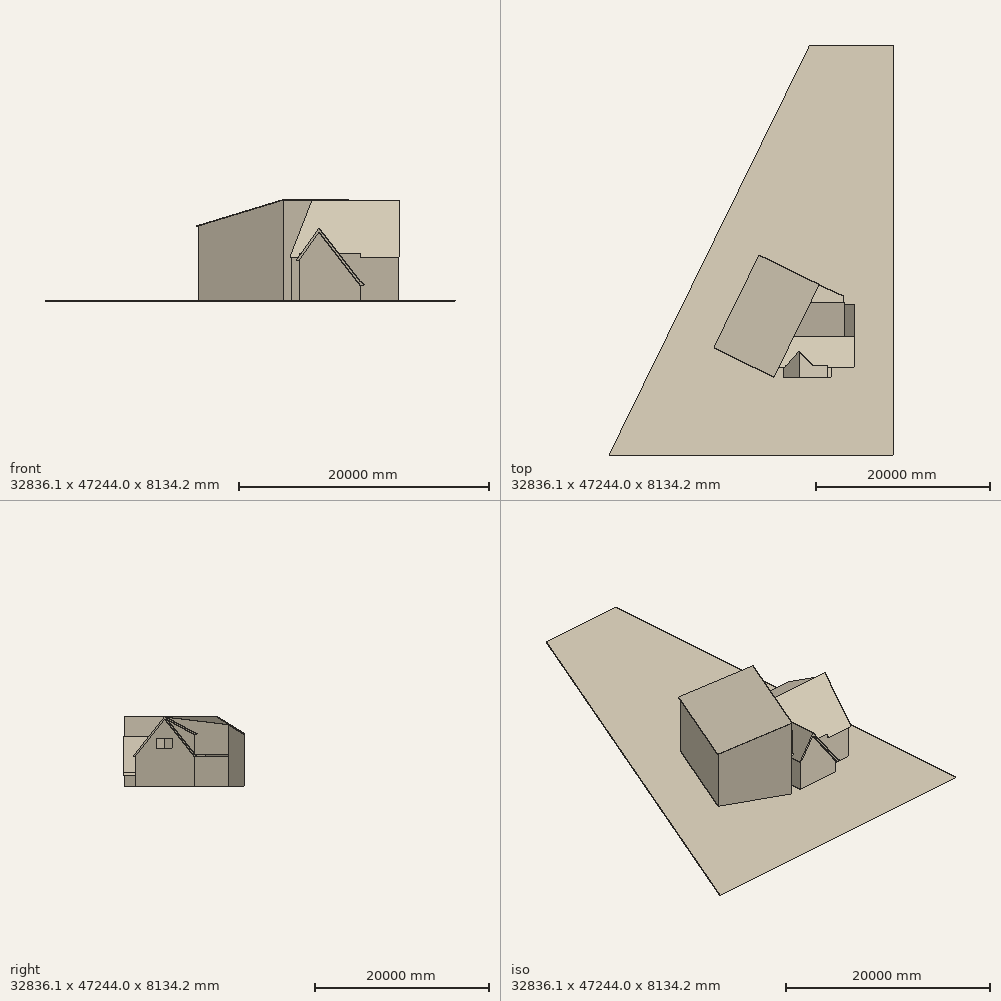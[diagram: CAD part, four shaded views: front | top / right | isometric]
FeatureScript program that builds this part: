
annotation { "Feature Type Name" : "Feature", "Feature Type Description" : "" }
export const myFeature = defineFeature(function(context is Context, id is Id, definition is map)
    precondition{}
    {
        {
            var Q0;
            Q0=qCreatedBy(makeId("Top.planeOp"),FACE);
            var sketch = newSketch(context, id + "F0", { "sketchPlane" : qUnion([Q0])});
            skLineSegment(sketch, "E0", {"start": v(0, 47244) * mm, "end": v(0, 0) * mm});
            skLineSegment(sketch, "E1", {"start": v(0, 0) * mm, "end": v(-32836.1, 0) * mm});
            skLineSegment(sketch, "E2", {"start": v(-32836.1, 0) * mm, "end": v(-9704.83, 47244) * mm});
            skLineSegment(sketch, "E3", {"start": v(-9704.83, 47244) * mm, "end": v(0, 47244) * mm});
            skSolve(sketch);
        }
        {
            var Q0;
            Q0=makeQuery(id+"F0.imprint","IMPRINT",FACE,{"disambiguationData":[TD([[makeQuery(id+"F0.imprint","IMPRINT",EDGE,{"derivedFrom":sQuery(id+"F0.wireOp",EDGE,"E0")}),-1.0]])]});
            extrude(context, id + "F1", {"entities" : qUnion([Q0]), "depth" : 25.4 * mm});
        }
        {
            var Q0;
            Q0=makeQuery(id+"F1.opExtrude","CAP_FACE",FACE,{"disambiguationData":[OSD([sQuery(id+"F0.wireOp",EDGE,"E0"),sQuery(id+"F0.wireOp",EDGE,"E1"),sQuery(id+"F0.wireOp",EDGE,"E2"),sQuery(id+"F0.wireOp",EDGE,"E3")])],"isStart":false});
            var sketch = newSketch(context, id + "F2", { "sketchPlane" : qUnion([Q0])});
            skLineSegment(sketch, "E4.bottom", {"start": v(-13197.84, 17160.24) * mm, "end": v(-4572, 17160.24) * mm});
            skLineSegment(sketch, "E4.top", {"start": v(-13197.84, 10363.2) * mm, "end": v(-4572, 10363.2) * mm});
            skLineSegment(sketch, "E4.left", {"start": v(-13197.84, 17160.24) * mm, "end": v(-13197.84, 10363.2) * mm});
            skLineSegment(sketch, "E4.right", {"start": v(-4572, 17160.24) * mm, "end": v(-4572, 10363.2) * mm});
            skLineSegment(sketch, "E5.bottom", {"start": v(-13045.44, 17007.84) * mm, "end": v(-4724.4, 17007.84) * mm});
            skLineSegment(sketch, "E5.top", {"start": v(-13045.44, 10515.6) * mm, "end": v(-4724.4, 10515.6) * mm});
            skLineSegment(sketch, "E5.left", {"start": v(-13045.44, 17007.84) * mm, "end": v(-13045.44, 10515.6) * mm});
            skLineSegment(sketch, "E5.right", {"start": v(-4724.4, 17007.84) * mm, "end": v(-4724.4, 10515.6) * mm});
            skSolve(sketch);
        }
        {
            var Q0;
            Q0=makeQuery(id+"F2.imprint","IMPRINT",FACE,{"disambiguationData":[TD([[makeQuery(id+"F2.imprint","IMPRINT",EDGE,{"derivedFrom":sQuery(id+"F2.wireOp",EDGE,"E4.bottom")}),-1.0]])]});
            extrude(context, id + "F3", {"entities" : qUnion([Q0]), "offsetDistance" : 30.48 * mm, "depth" : 7734 * mm});
        }
        {
            var Q0;
            Q0=makeQuery(id+"F1.opExtrude","CAP_FACE",FACE,{"disambiguationData":[OSD([sQuery(id+"F0.wireOp",EDGE,"E0"),sQuery(id+"F0.wireOp",EDGE,"E1"),sQuery(id+"F0.wireOp",EDGE,"E2"),sQuery(id+"F0.wireOp",EDGE,"E3")])],"isStart":false});
            var sketch = newSketch(context, id + "F4", { "sketchPlane" : qUnion([Q0])});
            skLineSegment(sketch, "E6", {"start": v(-13197.84, 17160.24) * mm, "end": v(-17465.04, 17160.24) * mm});
            skLineSegment(sketch, "E7", {"start": v(-17465.04, 17160.24) * mm, "end": v(-17465.04, 11064.24) * mm});
            skLineSegment(sketch, "E8", {"start": v(-17465.04, 11064.24) * mm, "end": v(-13197.84, 11064.24) * mm});
            skLineSegment(sketch, "E9", {"start": v(-13197.84, 17007.84) * mm, "end": v(-17312.64, 17007.84) * mm});
            skLineSegment(sketch, "E10", {"start": v(-17312.64, 17007.84) * mm, "end": v(-17312.64, 11216.64) * mm});
            skLineSegment(sketch, "E11", {"start": v(-17312.64, 11216.64) * mm, "end": v(-13197.84, 11216.64) * mm});
            skLineSegment(sketch, "E12", {"start": v(-13197.84, 17160.24) * mm, "end": v(-13197.84, 17007.84) * mm});
            skLineSegment(sketch, "E13", {"start": v(-10808.26, 7562.78) * mm, "end": v(-10586.18, 7562.78) * mm});
            skLineSegment(sketch, "E14", {"start": v(-13197.84, 11216.64) * mm, "end": v(-13197.84, 11064.24) * mm});
            skSolve(sketch);
        }
        {
            var Q0;
            Q0=makeQuery(id+"F4.imprint","IMPRINT",FACE,{"disambiguationData":[TD([[makeQuery(id+"F4.imprint","IMPRINT",EDGE,{"derivedFrom":sQuery(id+"F4.wireOp",EDGE,"E6")}),1.0]])]});
            extrude(context, id + "F5", {"entities" : qUnion([Q0]), "depth" : 3048 * mm});
        }
        {
            var Q0;
            Q0=makeQuery(id+"F1.opExtrude","CAP_FACE",FACE,{"disambiguationData":[OSD([sQuery(id+"F0.wireOp",EDGE,"E0"),sQuery(id+"F0.wireOp",EDGE,"E1"),sQuery(id+"F0.wireOp",EDGE,"E2"),sQuery(id+"F0.wireOp",EDGE,"E3")])],"isStart":false});
            var sketch = newSketch(context, id + "F6", { "sketchPlane" : qUnion([Q0])});
            skLineSegment(sketch, "E15", {"start": v(-12496.8, 10363.2) * mm, "end": v(-12496.8, 9144) * mm});
            skLineSegment(sketch, "E16", {"start": v(-12496.8, 9144) * mm, "end": v(-7620, 9144) * mm});
            skLineSegment(sketch, "E17", {"start": v(-7620, 9144) * mm, "end": v(-7620, 10363.2) * mm});
            skLineSegment(sketch, "E18", {"start": v(-7620, 10363.2) * mm, "end": v(-7772.4, 10363.2) * mm});
            skLineSegment(sketch, "E19", {"start": v(-7772.4, 10363.2) * mm, "end": v(-7772.4, 9296.4) * mm});
            skLineSegment(sketch, "E20", {"start": v(-7772.4, 9296.4) * mm, "end": v(-12344.4, 9296.4) * mm});
            skLineSegment(sketch, "E21", {"start": v(-12344.4, 9296.4) * mm, "end": v(-12344.4, 10363.2) * mm});
            skLineSegment(sketch, "E22", {"start": v(-12344.4, 10363.2) * mm, "end": v(-12496.8, 10363.2) * mm});
            skSolve(sketch);
        }
        {
            var Q0;
            Q0=makeQuery(id+"F6.imprint","IMPRINT",FACE,{"disambiguationData":[TD([[makeQuery(id+"F6.imprint","IMPRINT",EDGE,{"derivedFrom":sQuery(id+"F6.wireOp",EDGE,"E15")}),1.0]])]});
            extrude(context, id + "F7", {"entities" : qUnion([Q0]), "offsetDistance" : 30.48 * mm, "depth" : 5486.4 * mm});
        }
        {
            var Q0;
            Q0=makeQuery(id+"F3.opExtrude","SWEPT_FACE",FACE,{"disambiguationData":[OSD([sQuery(id+"F2.wireOp",EDGE,"E4.right")])]});
            var sketch = newSketch(context, id + "F8", { "sketchPlane" : qUnion([Q0])});
            skLineSegment(sketch, "E23", {"start": v(10363.2, 3479.79) * mm, "end": v(13761.72, 7759.4) * mm});
            skLineSegment(sketch, "E24", {"start": v(13761.72, 7759.4) * mm, "end": v(17160.24, 3479.79) * mm});
            skLineSegment(sketch, "E25", {"start": v(10363.2, 3479.79) * mm, "end": v(10363.2, 7759.4) * mm});
            skLineSegment(sketch, "E26", {"start": v(10363.2, 7759.4) * mm, "end": v(17160.24, 7759.4) * mm});
            skLineSegment(sketch, "E27", {"start": v(17160.24, 7759.4) * mm, "end": v(17160.24, 3479.79) * mm});
            skSolve(sketch);
        }
        {
            var Q0;
            {var subQ0=sQuery(id+"F8.wireOp",EDGE,"E24");Q0=makeQuery(id+"F8.imprint","IMPRINT",FACE,{"disambiguationData":[TD([[makeQuery(id+"F8.imprint","IMPRINT",EDGE,{"derivedFrom":subQ0}),1.0]])]});}
            var Q1;
            {var subQ0=sQuery(id+"F8.wireOp",EDGE,"E23");Q1=makeQuery(id+"F8.imprint","IMPRINT",FACE,{"disambiguationData":[TD([[makeQuery(id+"F8.imprint","IMPRINT",EDGE,{"derivedFrom":subQ0}),1.0]])]});}
            var Q2;
            Q2=makeQuery(id+"F3.opExtrude","SWEPT_FACE",FACE,{"disambiguationData":[OSD([sQuery(id+"F2.wireOp",EDGE,"E4.left")])]});
            extrude(context, id + "F9", {"entities" : qUnion([Q0, Q1]), "operationType" : NewBodyOperationType.REMOVE, "endBound" : BoundingType.UP_TO_SURFACE, "oppositeDirection" : true, "depth" : 30.48 * mm, "endBoundEntityFace" : qUnion([Q2]), "offsetDistance" : 30.48 * mm});
        }
        {
            var Q0;
            Q0=makeQuery(id+"F3.opExtrude","SWEPT_FACE",FACE,{"disambiguationData":[OSD([sQuery(id+"F2.wireOp",EDGE,"E4.right")])]});
            var sketch = newSketch(context, id + "F10", { "sketchPlane" : qUnion([Q0])});
            skLineSegment(sketch, "E28", {"start": v(10103.72, 3479.79) * mm, "end": v(13761.72, 8086.14) * mm});
            skLineSegment(sketch, "E29", {"start": v(13761.72, 8086.14) * mm, "end": v(17419.72, 3479.79) * mm});
            skLineSegment(sketch, "E30", {"start": v(17419.72, 3479.79) * mm, "end": v(17160.24, 3479.79) * mm});
            skLineSegment(sketch, "E31", {"start": v(17160.24, 3479.79) * mm, "end": v(13761.72, 7759.4) * mm});
            skLineSegment(sketch, "E32", {"start": v(13761.72, 7759.4) * mm, "end": v(10363.2, 3479.79) * mm});
            skLineSegment(sketch, "E33", {"start": v(10363.2, 3479.79) * mm, "end": v(10103.72, 3479.79) * mm});
            skSolve(sketch);
        }
        {
            var Q0;
            {var subQ6=sQuery(id+"F10.wireOp",EDGE,"E29");var subQ7=sQuery(id+"F10.wireOp",EDGE,"E28");var subQ8=makeQuery(id+"F10.imprint","INTERSECT",VERTEX,{"derivedFrom":[subQ7,subQ6]});Q0=makeQuery(id+"F10.imprint","IMPRINT",FACE,{"disambiguationData":[TD([[makeQuery(id+"F10.imprint","IMPRINT",EDGE,{"disambiguationData":[TD([[subQ8,1.0]])],"derivedFrom":subQ7}),-1.0]])]});}
            extrude(context, id + "F11", {"entities" : qUnion([Q0]), "operationType" : NewBodyOperationType.ADD, "depth" : 76.2 * mm, "offsetDistance" : 30.48 * mm, "hasSecondDirection" : true, "secondDirectionOppositeDirection" : true, "secondDirectionDepth" : 8702.04 * mm});
        }
        {
            var Q0;
            Q0=makeQuery(id+"F7.opExtrude","SWEPT_FACE",FACE,{"disambiguationData":[OSD([sQuery(id+"F6.wireOp",EDGE,"E16")])]});
            var sketch = newSketch(context, id + "F12", { "sketchPlane" : qUnion([Q0])});
            skLineSegment(sketch, "E34", {"start": v(-12496.8, 3276.6) * mm, "end": v(-10922.02, 5511.8) * mm});
            skLineSegment(sketch, "E35", {"start": v(-10922.02, 5511.8) * mm, "end": v(-7620, 1244.6) * mm});
            skLineSegment(sketch, "E36", {"start": v(-7620, 1244.6) * mm, "end": v(-7620, 5511.8) * mm});
            skLineSegment(sketch, "E37", {"start": v(-7620, 5511.8) * mm, "end": v(-12496.8, 5511.8) * mm});
            skLineSegment(sketch, "E38", {"start": v(-12496.8, 5511.8) * mm, "end": v(-12496.8, 3276.6) * mm});
            skSolve(sketch);
        }
        {
            var Q0;
            Q0=qSketchRegion(id+"F12",true);
            var Q1;
            Q1=makeQuery(id+"F7.opExtrude","SWEPT_FACE",FACE,{"disambiguationData":[OSD([sQuery(id+"F6.wireOp",EDGE,"E22")])]});
            var Q2;
            Q2=makeQuery(id+"F3.opExtrude","SWEPT_BODY",BODY,{"disambiguationData":[OSD([sQuery(id+"F2.wireOp",EDGE,"E4.bottom"),sQuery(id+"F2.wireOp",EDGE,"E4.top"),sQuery(id+"F2.wireOp",EDGE,"E4.left"),sQuery(id+"F2.wireOp",EDGE,"E4.right"),sQuery(id+"F2.wireOp",EDGE,"E5.bottom"),sQuery(id+"F2.wireOp",EDGE,"E5.top"),sQuery(id+"F2.wireOp",EDGE,"E5.left"),sQuery(id+"F2.wireOp",EDGE,"E5.right")])]});
            extrude(context, id + "F13", {"entities" : qUnion([Q0]), "operationType" : NewBodyOperationType.REMOVE, "endBound" : BoundingType.UP_TO_SURFACE, "oppositeDirection" : true, "depth" : 30.48 * mm, "endBoundEntityFace" : qUnion([Q1]), "endBoundEntityBody" : qUnion([Q2]), "offsetDistance" : 30.48 * mm});
        }
        {
            var Q0;
            Q0=makeQuery(id+"F7.opExtrude","SWEPT_FACE",FACE,{"disambiguationData":[OSD([sQuery(id+"F6.wireOp",EDGE,"E16")])]});
            var sketch = newSketch(context, id + "F14", { "sketchPlane" : qUnion([Q0])});
            skLineSegment(sketch, "E39", {"start": v(-10922.02, 5511.8) * mm, "end": v(-12496.8, 3276.6) * mm});
            skLineSegment(sketch, "E40", {"start": v(-12496.8, 3276.6) * mm, "end": v(-12730.73, 3276.6) * mm});
            skLineSegment(sketch, "E41", {"start": v(-12730.73, 3276.6) * mm, "end": v(-10922.02, 5843.83) * mm});
            skLineSegment(sketch, "E42", {"start": v(-10922.02, 5843.83) * mm, "end": v(-7670.8, 1642.28) * mm});
            skLineSegment(sketch, "E43", {"start": v(-7670.8, 1642.28) * mm, "end": v(-7213.6, 1244.6) * mm});
            skLineSegment(sketch, "E44", {"start": v(-7213.6, 1244.6) * mm, "end": v(-7620, 1244.6) * mm});
            skLineSegment(sketch, "E45", {"start": v(-7620, 1244.6) * mm, "end": v(-10922.02, 5511.8) * mm});
            skSolve(sketch);
        }
        {
            var Q0;
            Q0=makeQuery(id+"F14.imprint","IMPRINT",FACE,{"disambiguationData":[TD([[makeQuery(id+"F14.imprint","IMPRINT",EDGE,{"derivedFrom":sQuery(id+"F14.wireOp",EDGE,"E39")}),1.0]])]});
            var Q1;
            Q1=makeQuery(id+"F3.opExtrude","SWEPT_BODY",BODY,{"disambiguationData":[OSD([sQuery(id+"F2.wireOp",EDGE,"E4.bottom"),sQuery(id+"F2.wireOp",EDGE,"E4.top"),sQuery(id+"F2.wireOp",EDGE,"E4.left"),sQuery(id+"F2.wireOp",EDGE,"E4.right"),sQuery(id+"F2.wireOp",EDGE,"E5.bottom"),sQuery(id+"F2.wireOp",EDGE,"E5.top"),sQuery(id+"F2.wireOp",EDGE,"E5.left"),sQuery(id+"F2.wireOp",EDGE,"E5.right")])]});
            var Q2;
            Q2=makeQuery(id+"F3.opExtrude","SWEPT_BODY",BODY,{"disambiguationData":[OSD([sQuery(id+"F2.wireOp",EDGE,"E4.bottom"),sQuery(id+"F2.wireOp",EDGE,"E4.top"),sQuery(id+"F2.wireOp",EDGE,"E4.left"),sQuery(id+"F2.wireOp",EDGE,"E4.right"),sQuery(id+"F2.wireOp",EDGE,"E5.bottom"),sQuery(id+"F2.wireOp",EDGE,"E5.top"),sQuery(id+"F2.wireOp",EDGE,"E5.left"),sQuery(id+"F2.wireOp",EDGE,"E5.right")])]});
            extrude(context, id + "F15", {"entities" : qUnion([Q0]), "depth" : 152.4 * mm, "endBoundEntityBody" : qUnion([Q1]), "offsetDistance" : 30.48 * mm, "hasSecondDirection" : true, "secondDirectionBound" : SecondDirectionBoundingType.UP_TO_BODY, "secondDirectionOppositeDirection" : true, "secondDirectionDepth" : 152.4 * mm, "secondDirectionBoundEntityBody" : qUnion([Q2])});
        }
        {
            var Q0;
            Q0=qCreatedBy(makeId("Top.planeOp"),FACE);
            cPlane(context, id + "F16", {"entities" : qUnion([Q0]), "cplaneType" : CPlaneType.OFFSET, "offset" : 12192 * mm, "width" : 152.4 * mm, "height" : 152.4 * mm});
        }
        {
            var Q0;
            Q0=qCreatedBy(id+"F16.planeOp",FACE);
            var sketch = newSketch(context, id + "F17", { "sketchPlane" : qUnion([Q0])});
            skLineSegment(sketch, "E46", {"start": v(-11978.64, 17160.24) * mm, "end": v(-5791.2, 17160.24) * mm});
            skLineSegment(sketch, "E47", {"start": v(-5791.2, 17160.24) * mm, "end": v(-5791.2, 13761.72) * mm});
            skLineSegment(sketch, "E48", {"start": v(-5791.2, 13761.72) * mm, "end": v(-6019.8, 13761.72) * mm});
            skLineSegment(sketch, "E49", {"start": v(-6019.8, 13761.72) * mm, "end": v(-6019.8, 17007.84) * mm});
            skLineSegment(sketch, "E50", {"start": v(-6019.8, 17007.84) * mm, "end": v(-11750.04, 17007.84) * mm});
            skLineSegment(sketch, "E51", {"start": v(-11750.04, 17007.84) * mm, "end": v(-11750.04, 13761.72) * mm});
            skLineSegment(sketch, "E52", {"start": v(-11750.04, 13761.72) * mm, "end": v(-11978.64, 13761.72) * mm});
            skLineSegment(sketch, "E53", {"start": v(-11978.64, 13761.72) * mm, "end": v(-11978.64, 17160.24) * mm});
            skSolve(sketch);
        }
        {
            var Q0;
            Q0=makeQuery(id+"F17.imprint","IMPRINT",FACE,{"disambiguationData":[TD([[makeQuery(id+"F17.imprint","IMPRINT",EDGE,{"derivedFrom":sQuery(id+"F17.wireOp",EDGE,"E46")}),-1.0]])]});
            var Q1;
            Q1=makeQuery(id+"F3.opExtrude","SWEPT_BODY",BODY,{"disambiguationData":[OSD([sQuery(id+"F2.wireOp",EDGE,"E4.bottom"),sQuery(id+"F2.wireOp",EDGE,"E4.top"),sQuery(id+"F2.wireOp",EDGE,"E4.left"),sQuery(id+"F2.wireOp",EDGE,"E4.right"),sQuery(id+"F2.wireOp",EDGE,"E5.bottom"),sQuery(id+"F2.wireOp",EDGE,"E5.top"),sQuery(id+"F2.wireOp",EDGE,"E5.left"),sQuery(id+"F2.wireOp",EDGE,"E5.right")])]});
            extrude(context, id + "F18", {"entities" : qUnion([Q0]), "operationType" : NewBodyOperationType.ADD, "endBound" : BoundingType.UP_TO_BODY, "oppositeDirection" : true, "depth" : 30.48 * mm, "endBoundEntityBody" : qUnion([Q1]), "offsetDistance" : 30.48 * mm});
        }
        {
            var Q0;
            Q0=makeQuery(id+"F18.opExtrude","SWEPT_FACE",FACE,{"disambiguationData":[OSD([sQuery(id+"F17.wireOp",EDGE,"E47")])]});
            var sketch = newSketch(context, id + "F19", { "sketchPlane" : qUnion([Q0])});
            skLineSegment(sketch, "E54", {"start": v(13761.72, 8086.14) * mm, "end": v(17160.24, 6019.8) * mm});
            skLineSegment(sketch, "E55", {"start": v(17160.24, 6019.8) * mm, "end": v(17160.24, 12192) * mm});
            skLineSegment(sketch, "E56", {"start": v(17160.24, 12192) * mm, "end": v(13761.72, 12192) * mm});
            skLineSegment(sketch, "E57", {"start": v(13761.72, 12192) * mm, "end": v(13761.72, 8086.14) * mm});
            skSolve(sketch);
        }
        {
            var Q0;
            {var subQ5=sQuery(id+"F19.wireOp",EDGE,"E55");Q0=makeQuery(id+"F19.imprint","IMPRINT",FACE,{"disambiguationData":[TD([[makeQuery(id+"F19.imprint","IMPRINT",EDGE,{"derivedFrom":subQ5}),1.0]])]});}
            var Q1;
            Q1=makeQuery(id+"F18.opExtrude","SWEPT_FACE",FACE,{"disambiguationData":[OSD([sQuery(id+"F17.wireOp",EDGE,"E53")])]});
            extrude(context, id + "F20", {"entities" : qUnion([Q0]), "operationType" : NewBodyOperationType.REMOVE, "endBound" : BoundingType.UP_TO_SURFACE, "oppositeDirection" : true, "depth" : 30.48 * mm, "endBoundEntityFace" : qUnion([Q1]), "offsetDistance" : 30.48 * mm});
        }
        {
            var Q0;
            Q0=makeQuery(id+"F18.opExtrude","SWEPT_FACE",FACE,{"disambiguationData":[OSD([sQuery(id+"F17.wireOp",EDGE,"E47")])]});
            var sketch = newSketch(context, id + "F21", { "sketchPlane" : qUnion([Q0])});
            skLineSegment(sketch, "E58", {"start": v(13761.72, 7855.2) * mm, "end": v(17160.24, 6019.8) * mm});
            skLineSegment(sketch, "E59", {"start": v(17160.24, 6019.8) * mm, "end": v(17587.86, 6019.8) * mm});
            skLineSegment(sketch, "E60", {"start": v(17587.86, 6019.8) * mm, "end": v(13761.72, 8086.14) * mm});
            skLineSegment(sketch, "E61", {"start": v(13761.72, 8086.14) * mm, "end": v(13761.72, 7855.2) * mm});
            skSolve(sketch);
        }
        {
            var Q0;
            Q0=qSketchRegion(id+"F21",true);
            extrude(context, id + "F22", {"entities" : qUnion([Q0]), "operationType" : NewBodyOperationType.ADD, "depth" : 76.2 * mm, "offsetDistance" : 30.48 * mm, "hasSecondDirection" : true, "secondDirectionOppositeDirection" : true, "secondDirectionDepth" : 6263.64 * mm});
        }
        {
            var Q0;
            Q0=makeQuery(id+"F18.opExtrude","SWEPT_FACE",FACE,{"disambiguationData":[OSD([sQuery(id+"F17.wireOp",EDGE,"E47")])]});
            var sketch = newSketch(context, id + "F23", { "sketchPlane" : qUnion([Q0])});
            skLineSegment(sketch, "E62", {"start": v(17160.24, 3479.79) * mm, "end": v(17160.24, 3806.54) * mm});
            skLineSegment(sketch, "E63", {"start": v(17160.24, 3806.54) * mm, "end": v(17419.72, 3479.79) * mm});
            skLineSegment(sketch, "E64", {"start": v(17419.72, 3479.79) * mm, "end": v(17160.24, 3479.79) * mm});
            skSolve(sketch);
        }
        {
            var Q0;
            Q0=makeQuery(id+"F23.imprint","IMPRINT",FACE,{"disambiguationData":[TD([[makeQuery(id+"F23.imprint","IMPRINT",EDGE,{"derivedFrom":sQuery(id+"F23.wireOp",EDGE,"E62")}),-1.0]])]});
            var Q1;
            Q1=makeQuery(id+"F18.opExtrude","SWEPT_FACE",FACE,{"disambiguationData":[OSD([sQuery(id+"F17.wireOp",EDGE,"E53")])]});
            extrude(context, id + "F24", {"entities" : qUnion([Q0]), "operationType" : NewBodyOperationType.REMOVE, "endBound" : BoundingType.UP_TO_SURFACE, "oppositeDirection" : true, "depth" : 3048 * mm, "endBoundEntityFace" : qUnion([Q1]), "offsetDistance" : 30.48 * mm});
        }
        {
            var Q0;
            Q0=makeQuery(id+"F1.opExtrude","CAP_FACE",FACE,{"disambiguationData":[OSD([sQuery(id+"F0.wireOp",EDGE,"E0"),sQuery(id+"F0.wireOp",EDGE,"E1"),sQuery(id+"F0.wireOp",EDGE,"E2"),sQuery(id+"F0.wireOp",EDGE,"E3")])],"isStart":false});
            var sketch = newSketch(context, id + "F25", { "sketchPlane" : qUnion([Q0])});
            skLineSegment(sketch, "E65", {"start": v(-11483.04, 13761.72) * mm, "end": v(-13743.93, 9144) * mm});
            skLineSegment(sketch, "E66", {"start": v(-13743.93, 9144) * mm, "end": v(-20587.66, 12494.78) * mm});
            skLineSegment(sketch, "E67", {"start": v(-20587.66, 12494.78) * mm, "end": v(-15494.48, 22897.25) * mm});
            skLineSegment(sketch, "E68", {"start": v(-15494.48, 22897.25) * mm, "end": v(-11750.04, 21063.93) * mm});
            skLineSegment(sketch, "E69", {"start": v(-11750.04, 21063.93) * mm, "end": v(-11750.04, 13761.72) * mm});
            skLineSegment(sketch, "E70", {"start": v(-11978.64, 13761.72) * mm, "end": v(-11978.64, 20921.32) * mm});
            skLineSegment(sketch, "E71", {"start": v(-11978.64, 20921.32) * mm, "end": v(-15389.7, 22591.42) * mm});
            skLineSegment(sketch, "E72", {"start": v(-15389.7, 22591.42) * mm, "end": v(-20281.83, 12599.57) * mm});
            skLineSegment(sketch, "E73", {"start": v(-20281.83, 12599.57) * mm, "end": v(-13848.72, 9449.84) * mm});
            skLineSegment(sketch, "E74", {"start": v(-13848.72, 9449.84) * mm, "end": v(-11737.57, 13761.72) * mm});
            skLineSegment(sketch, "E75", {"start": v(-11978.64, 13761.72) * mm, "end": v(-11750.04, 13761.72) * mm});
            skLineSegment(sketch, "E76", {"start": v(-11737.57, 13761.72) * mm, "end": v(-11483.04, 13761.72) * mm});
            skSolve(sketch);
        }
        {
            var Q0;
            Q0=makeQuery(id+"F25.imprint","IMPRINT",FACE,{"disambiguationData":[TD([[makeQuery(id+"F25.imprint","IMPRINT",EDGE,{"derivedFrom":sQuery(id+"F25.wireOp",EDGE,"E65")}),-1.0]])]});
            extrude(context, id + "F26", {"entities" : qUnion([Q0]), "depth" : 10363.2 * mm, "offsetDistance" : 30.48 * mm});
        }
        {
            var Q0;
            Q0=makeQuery(id+"F26.opExtrude","SWEPT_FACE",FACE,{"disambiguationData":[OSD([sQuery(id+"F25.wireOp",EDGE,"E66")])]});
            var sketch = newSketch(context, id + "F27", { "sketchPlane" : qUnion([Q0])});
            skLineSegment(sketch, "E77", {"start": v(-16364.74, 10388.6) * mm, "end": v(-23984.74, 10388.6) * mm});
            skLineSegment(sketch, "E78", {"start": v(-23984.74, 10388.6) * mm, "end": v(-23984.74, 6019.78) * mm});
            skLineSegment(sketch, "E79", {"start": v(-23984.74, 6019.78) * mm, "end": v(-16364.74, 8102.6) * mm});
            skLineSegment(sketch, "E80", {"start": v(-16364.74, 8102.6) * mm, "end": v(-16364.74, 10388.6) * mm});
            skSolve(sketch);
        }
        {
            var Q0;
            Q0=makeQuery(id+"F27.imprint","IMPRINT",FACE,{"disambiguationData":[TD([[makeQuery(id+"F27.imprint","IMPRINT",EDGE,{"derivedFrom":sQuery(id+"F27.wireOp",EDGE,"E77")}),1.0]])]});
            var Q1;
            Q1=makeQuery(id+"F26.opExtrude","SWEPT_FACE",FACE,{"disambiguationData":[OSD([sQuery(id+"F25.wireOp",EDGE,"E68")])]});
            extrude(context, id + "F28", {"entities" : qUnion([Q0]), "operationType" : NewBodyOperationType.REMOVE, "endBound" : BoundingType.UP_TO_SURFACE, "oppositeDirection" : true, "depth" : 30.48 * mm, "endBoundEntityFace" : qUnion([Q1]), "offsetDistance" : 30.48 * mm});
        }
        {
            var Q0;
            Q0=makeQuery(id+"F26.opExtrude","SWEPT_FACE",FACE,{"disambiguationData":[OSD([sQuery(id+"F25.wireOp",EDGE,"E66")])]});
            var sketch = newSketch(context, id + "F29", { "sketchPlane" : qUnion([Q0])});
            skLineSegment(sketch, "E81", {"start": v(-16364.74, 8102.6) * mm, "end": v(-16364.74, 8134.2) * mm});
            skLineSegment(sketch, "E82", {"start": v(-16364.74, 8134.2) * mm, "end": v(-24100.34, 6019.78) * mm});
            skLineSegment(sketch, "E83", {"start": v(-24100.34, 6019.78) * mm, "end": v(-23984.74, 6019.78) * mm});
            skLineSegment(sketch, "E84", {"start": v(-23984.74, 6019.78) * mm, "end": v(-16364.74, 8102.6) * mm});
            skSolve(sketch);
        }
        {
            var Q0;
            Q0=makeQuery(id+"F29.imprint","IMPRINT",FACE,{"disambiguationData":[TD([[makeQuery(id+"F29.imprint","IMPRINT",EDGE,{"derivedFrom":sQuery(id+"F29.wireOp",EDGE,"E81")}),1.0]])]});
            extrude(context, id + "F30", {"entities" : qUnion([Q0]), "depth" : 152.4 * mm, "offsetDistance" : 30.48 * mm, "hasSecondDirection" : true, "secondDirectionOppositeDirection" : true, "secondDirectionDepth" : 11734.8 * mm});
        }
        {
            var Q0;
            Q0=qCreatedBy(id+"F16.planeOp",FACE);
            var sketch = newSketch(context, id + "F31", { "sketchPlane" : qUnion([Q0])});
            skLineSegment(sketch, "E85", {"start": v(-11750.04, 13765.6) * mm, "end": v(-11750.04, 21368.73) * mm});
            skLineSegment(sketch, "E86", {"start": v(-11750.04, 21368.73) * mm, "end": v(-5715, 21368.73) * mm});
            skLineSegment(sketch, "E87", {"start": v(-5715, 21368.73) * mm, "end": v(-5715, 13765.6) * mm});
            skLineSegment(sketch, "E88", {"start": v(-5715, 13765.6) * mm, "end": v(-11750.04, 13765.6) * mm});
            skSolve(sketch);
        }
        {
            var Q0;
            Q0=qCreatedBy(id+"F16.planeOp",FACE);
            var sketch = newSketch(context, id + "F32", { "sketchPlane" : qUnion([Q0])});
            skLineSegment(sketch, "E89", {"start": v(-11750.04, 13761.72) * mm, "end": v(-11750.04, 21063.93) * mm});
            skLineSegment(sketch, "E90", {"start": v(-11750.04, 13761.72) * mm, "end": v(-10922.02, 13761.72) * mm});
            skLineSegment(sketch, "E91", {"start": v(-10922.02, 21063.93) * mm, "end": v(-10922.02, 13761.72) * mm});
            skLineSegment(sketch, "E92", {"start": v(-10922.02, 21063.93) * mm, "end": v(-11750.04, 21063.93) * mm});
            skSolve(sketch);
        }
        {
            var Q0;
            Q0=makeQuery(id+"F3.opExtrude","SWEPT_FACE",FACE,{"disambiguationData":[OSD([sQuery(id+"F2.wireOp",EDGE,"E4.right")])]});
            var sketch = newSketch(context, id + "F33", { "sketchPlane" : qUnion([Q0])});
            skLineSegment(sketch, "E93.bottom", {"start": v(12801.6, 5588) * mm, "end": v(14630.4, 5588) * mm});
            skLineSegment(sketch, "E93.top", {"start": v(12801.6, 4368.8) * mm, "end": v(14630.4, 4368.8) * mm});
            skLineSegment(sketch, "E93.left", {"start": v(12801.6, 5588) * mm, "end": v(12801.6, 4368.8) * mm});
            skLineSegment(sketch, "E93.right", {"start": v(14630.4, 5588) * mm, "end": v(14630.4, 4368.8) * mm});
            skSolve(sketch);
        }
        {
            var Q0;
            Q0=makeQuery(id+"F33.imprint","IMPRINT",FACE,{"disambiguationData":[TD([[makeQuery(id+"F33.imprint","IMPRINT",EDGE,{"derivedFrom":sQuery(id+"F33.wireOp",EDGE,"E93.bottom")}),-1.0]])]});
            extrude(context, id + "F34", {"entities" : qUnion([Q0]), "operationType" : NewBodyOperationType.REMOVE, "endBound" : BoundingType.UP_TO_NEXT, "oppositeDirection" : true, "depth" : 30.48 * mm, "offsetDistance" : 30.48 * mm});
        }
        {
            var Q0;
            Q0=makeQuery(id+"F1.opExtrude","CAP_FACE",FACE,{"disambiguationData":[OSD([sQuery(id+"F0.wireOp",EDGE,"E0"),sQuery(id+"F0.wireOp",EDGE,"E1"),sQuery(id+"F0.wireOp",EDGE,"E2"),sQuery(id+"F0.wireOp",EDGE,"E3")])],"isStart":false});
            var Q1;
            Q1=makeQuery(id+"F24.boolean.opBoolean","COPY",VERTEX,{"derivedFrom":makeQuery(id+"F24.opExtrude","CAP_VERTEX",VERTEX,{"disambiguationData":[OSD([sQuery(id+"F23.wireOp",EDGE,"E63"),sQuery(id+"F23.wireOp",EDGE,"E64")])],"isStart":true})});
            cPlane(context, id + "F35", {"entities" : qUnion([Q0, Q1]), "cplaneType" : CPlaneType.PLANE_POINT, "offset" : 25.4 * mm, "width" : 152.4 * mm, "height" : 152.4 * mm});
        }
        {
            var Q0;
            Q0=qCreatedBy(id+"F35.planeOp",FACE);
            var sketch = newSketch(context, id + "F36", { "sketchPlane" : qUnion([Q0])});
            skLineSegment(sketch, "E94", {"start": v(-11750.04, 17160.24) * mm, "end": v(-11750.04, 21063.93) * mm});
            skLineSegment(sketch, "E95", {"start": v(-11750.04, 21063.93) * mm, "end": v(-5843.05, 18379.44) * mm});
            skLineSegment(sketch, "E96", {"start": v(-5843.05, 18379.44) * mm, "end": v(-5843.05, 17160.24) * mm});
            skLineSegment(sketch, "E97", {"start": v(-5843.05, 17160.24) * mm, "end": v(-11750.04, 17160.24) * mm});
            skSolve(sketch);
        }
        {
            var Q0;
            Q0=makeQuery(id+"F36.imprint","IMPRINT",FACE,{"disambiguationData":[TD([[makeQuery(id+"F36.imprint","IMPRINT",EDGE,{"derivedFrom":sQuery(id+"F36.wireOp",EDGE,"E94")}),-1.0]])]});
            extrude(context, id + "F37", {"entities" : qUnion([Q0]), "depth" : 203.2 * mm, "offsetDistance" : 30.48 * mm});
        }
    });
